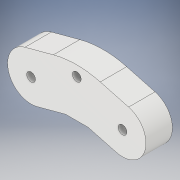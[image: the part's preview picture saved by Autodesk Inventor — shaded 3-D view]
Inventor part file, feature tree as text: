
AUTODESK INVENTOR PART (.ipt)
format: ipt  version: 2017 SP1 (Build 210196100, 196)  size: 120,832 bytes
history: native  units: in
note: dims shown in document units (in); Inventor stores cm internally (conversion verified against a paired STEP export)
features: extrude x1, sketch x1
ambient origin geometry x8: Origin, YZ Plane, XZ Plane, XY Plane, X Axis, Y Axis, Z Axis, Center Point
bodies: Solid1 (feature_tree)
feature tree (2):
  extrude  "Extrusion1"  Depth=0.3543in
  sketch  "Sketch1"  dims[d0=0.6299in d1=0.6299in d2=0.6299in d3=0.3937in d4=0.3937in d5=0.6299in d6=0.6299in d7=75.0deg d8=0.1181in d9=0.1181in d10=0.1181in d11=0.5118in d12=0.3543in d13=0.0in]
